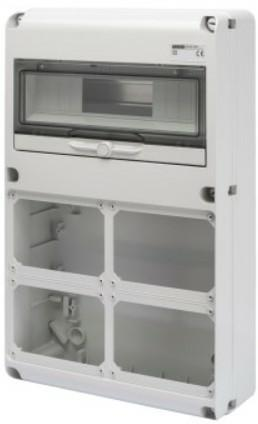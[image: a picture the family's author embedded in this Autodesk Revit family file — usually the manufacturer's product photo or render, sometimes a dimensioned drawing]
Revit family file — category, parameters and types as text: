
# Revit family: Building-IEC309Boards-GEWISS-68QDIN-DISTRIBUTION-BOARD-14MOD_4SOCKET-OUTLETS_IB_ORIZ
name_source: partatom
category: Apparecchi elettrici
units: mm (PartAtom-declared; Revit-internal decimal feet)

## family parameters
Condiviso = No
Host = Superficie
Mantenere orientamento annotazione = Sì
Punto di calcolo locali = Sì
Quota connettore circolare = Usa diametro
Taglio con vuoti quando caricato = No
Tipo di parte = Normale

## types (1)
- GW68009N - Q-DIN 14M 4 FLANGES S.O.BL.HOR.SBF IP65
    Accordance with Standards = EN 60208 - EN 60670-1 - IEC 60670-24
    Catalogue = BUILDING
    Catalogue Range = 68 QDIN
    Colour = Grey RAL 7035
    Descrizione = Q-DIN 14M 4 FLANGES S.O.BL.HOR.SBF IP65
    Dispersible power A (W) = 24
    Dispersible power B (W) = 64
    EAN code = 8011564744806
    Electrocod = 2242
    Glow Wire Test = 650°C
    Houseable interloc. socket. = 4 IB Horiz. 16/32A SBF IP44
    Houseable socket = 4 IB Horiz. 16/32A SBF IP44
    IDF = c071aca0-7753-4d09-bf42-5b742313563d
    IDT = 99915e0d-742e-4288-be31-3e8f2e4a73df
    IP degree = IP65
    Immagine tipo = GW68009N.jpg
    Installation type = Surface-mounting
    Insulation class = II
    L_Moduli = 266 mm  [stored 0.872703 ft]
    Modello = GW68009N
    N_Moduli = 14 mm  [stored 0.0459318 ft]
    No. IB socket-outlets houseable = 4 IB Horiz. 16/32A SBF IP44
    No. of blank lids supplied = 2 IB 16/32A
    No. of modules EN 50022 = 14
    No. of provided blank lids = 2 IB 16/32A
    Operating temperature: = -25 +40 °C
    POMELLO = bianco
    PRESA = rosso
    Produttore = GEWISS S.p.A.
    Prospetto di default = 1219 mm
    SEO = Board
    STRUTTURA = RAL - 7035
    STRUTTURA ALTA = Poche
    Shock resistance = IK08
    Spostamento_S = 1000 mm  [stored 3.28084 ft]
    Technical sheet = https://www.gewiss.com
    Thermo-pressure with ball = 70
    URL = https://www.gewiss.com
    VETRO = Vetro
    Version file RFA = 21.5
    Version type = Empty
    Working temperature = -25 ÷ +40 °C

note: source unit labels omitted for Thermo-pressure with ball — the stored unit's dimension contradicts the parameter name (converter mislabeling)

note: [stored X ft] marks values corroborated as IEEE doubles in the binary element streams (Revit-internal decimal feet)

## geometry (parser evidence)
native form markers: Sweep x4
no freeform markers — native parametric forms only
